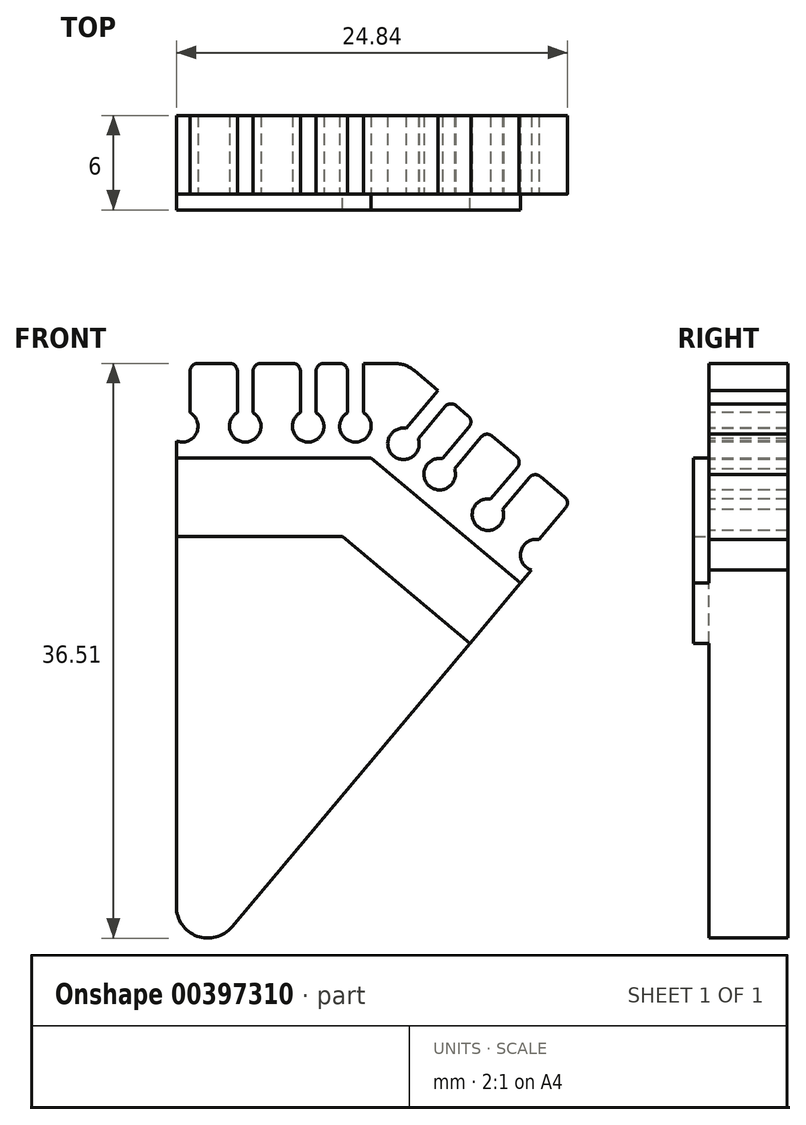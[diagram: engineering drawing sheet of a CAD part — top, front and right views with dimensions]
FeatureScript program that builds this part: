
annotation { "Feature Type Name" : "Feature", "Feature Type Description" : "" }
export const myFeature = defineFeature(function(context is Context, id is Id, definition is map)
    precondition{}
    {
        {
            var Q0;
            Q0=qCreatedBy(makeId("Front.planeOp"),FACE);
            var sketch = newSketch(context, id + "F0", { "sketchPlane" : qUnion([Q0])});
            skLineSegment(sketch, "E0.bottom", {"start": v(0, 0) * mm, "end": v(14.56, 0) * mm});
            skLineSegment(sketch, "E0.top", {"start": v(0, 40) * mm, "end": v(14.56, 40) * mm});
            skLineSegment(sketch, "E0.left", {"start": v(0, 0) * mm, "end": v(0, 40) * mm});
            skLineSegment(sketch, "E0.right", {"start": v(14.56, 0) * mm, "end": v(14.56, 40) * mm});
            skLineSegment(sketch, "E1", {"start": v(0, 0) * mm, "end": v(14.56, 40) * mm});
            skLineSegment(sketch, "E2", {"start": v(0, 34) * mm, "end": v(12.37, 34) * mm});
            skLineSegment(sketch, "E3", {"start": v(0, 29) * mm, "end": v(10.56, 29) * mm});
            skLineSegment(sketch, "E4", {"start": v(0, 38) * mm, "end": v(14.56, 38) * mm, "construction": true});
            skLineSegment(sketch, "E5", {"start": v(0, 36) * mm, "end": v(14.56, 36) * mm, "construction": true});
            skLineSegment(sketch, "E6", {"start": v(12.37, 34) * mm, "end": v(12.37, 40) * mm, "construction": true});
            skLineSegment(sketch, "E7", {"start": v(8.37, 34) * mm, "end": v(8.37, 40) * mm, "construction": true});
            skLineSegment(sketch, "E8", {"start": v(4.37, 34) * mm, "end": v(4.37, 40) * mm, "construction": true});
            skLineSegment(sketch, "E9", {"start": v(0.37, 34) * mm, "end": v(0.37, 40) * mm, "construction": true});
            skPoint(sketch, "E10", {"position": v(8.37, 36) * mm});
            skPoint(sketch, "E11", {"position": v(4.37, 36) * mm});
            skPoint(sketch, "E12", {"position": v(0.37, 36) * mm});
            skLineSegment(sketch, "E13", {"start": v(11.37, 34) * mm, "end": v(11.37, 40) * mm, "construction": true});
            skPoint(sketch, "E14", {"position": v(11.37, 36) * mm});
            skSolve(sketch);
        }
        {
            var Q0;
            Q0=qCreatedBy(makeId("Front.planeOp"),FACE);
            var sketch = newSketch(context, id + "F1", { "sketchPlane" : qUnion([Q0])});
            skCircle(sketch, "E15", {"center": v(11.37, 36) * mm, "radius": 1 * mm});
            skCircle(sketch, "E16", {"center": v(8.37, 36) * mm, "radius": 1 * mm});
            skCircle(sketch, "E17", {"center": v(0.37, 36) * mm, "radius": 1 * mm});
            skCircle(sketch, "E18", {"center": v(4.37, 36) * mm, "radius": 1 * mm});
            skLineSegment(sketch, "E19", {"start": v(10.87, 36.87) * mm, "end": v(10.87, 40) * mm});
            skLineSegment(sketch, "E20.MirrorCS", {"start": v(11.87, 36.87) * mm, "end": v(11.87, 40) * mm});
            skLineSegment(sketch, "E21", {"start": v(0.87, 36.87) * mm, "end": v(0.87, 40) * mm});
            skLineSegment(sketch, "E22", {"start": v(4.87, 36.87) * mm, "end": v(4.87, 40) * mm});
            skLineSegment(sketch, "E23.MirrorCS", {"start": v(3.87, 36.87) * mm, "end": v(3.87, 40) * mm});
            skLineSegment(sketch, "E24.MirrorCS", {"start": v(-0.13, 36.87) * mm, "end": v(-0.13, 40) * mm});
            skLineSegment(sketch, "E25", {"start": v(-0.13, 40) * mm, "end": v(0.87, 40) * mm});
            skLineSegment(sketch, "E26", {"start": v(3.87, 40) * mm, "end": v(4.87, 40) * mm});
            skLineSegment(sketch, "E27", {"start": v(7.87, 40) * mm, "end": v(8.87, 40) * mm});
            skLineSegment(sketch, "E28", {"start": v(10.87, 40) * mm, "end": v(11.87, 40) * mm});
            skLineSegment(sketch, "E29", {"start": v(8.87, 40) * mm, "end": v(8.87, 36.87) * mm});
            skLineSegment(sketch, "E30", {"start": v(7.87, 40) * mm, "end": v(7.87, 36.87) * mm});
            skSolve(sketch);
        }
        {
            var Q0;
            {var subQ3=sQuery(id+"F0.wireOp",EDGE,"E3");Q0=makeQuery(id+"F0.imprint","IMPRINT",FACE,{"disambiguationData":[TD([[makeQuery(id+"F0.imprint","IMPRINT",EDGE,{"derivedFrom":subQ3}),-1.0]])]});}
            var Q1;
            {var subQ0=sQuery(id+"F0.wireOp",EDGE,"E2");Q1=makeQuery(id+"F0.imprint","IMPRINT",FACE,{"disambiguationData":[TD([[makeQuery(id+"F0.imprint","IMPRINT",EDGE,{"derivedFrom":subQ0}),-1.0]])]});}
            var Q2;
            {var subQ0=sQuery(id+"F0.wireOp",EDGE,"E0.top");Q2=makeQuery(id+"F0.imprint","IMPRINT",FACE,{"disambiguationData":[TD([[makeQuery(id+"F0.imprint","IMPRINT",EDGE,{"derivedFrom":subQ0}),-1.0]])]});}
            extrude(context, id + "F2", {"entities" : qUnion([Q0, Q1, Q2]), "oppositeDirection" : true, "depth" : 5 * mm});
        }
        {
            var Q0;
            {var subQ0=sQuery(id+"F0.wireOp",EDGE,"E2");Q0=makeQuery(id+"F0.imprint","IMPRINT",FACE,{"disambiguationData":[TD([[makeQuery(id+"F0.imprint","IMPRINT",EDGE,{"derivedFrom":subQ0}),-1.0]])]});}
            extrude(context, id + "F3", {"entities" : qUnion([Q0]), "depth" : 1 * mm});
        }
        {
            var Q0;
            {var subQ0=sQuery(id+"F1.wireOp",EDGE,"E17");var subQ1=makeQuery(id+"F1.imprint","INTERSECT",VERTEX,{"derivedFrom":[subQ0,sQuery(id+"F1.wireOp",EDGE,"E21")]});Q0=makeQuery(id+"F1.imprint","IMPRINT",FACE,{"disambiguationData":[TD([[makeQuery(id+"F1.imprint","IMPRINT",EDGE,{"disambiguationData":[TD([[subQ1,-1.0]])],"derivedFrom":subQ0}),1.0]])]});}
            var Q1;
            {var subQ0=sQuery(id+"F1.wireOp",EDGE,"E21");Q1=makeQuery(id+"F1.imprint","IMPRINT",FACE,{"disambiguationData":[TD([[makeQuery(id+"F1.imprint","IMPRINT",EDGE,{"derivedFrom":subQ0}),1.0]])]});}
            var Q2;
            {var subQ0=sQuery(id+"F1.wireOp",EDGE,"E18");var subQ1=makeQuery(id+"F1.imprint","INTERSECT",VERTEX,{"derivedFrom":[subQ0,sQuery(id+"F1.wireOp",EDGE,"E22")]});Q2=makeQuery(id+"F1.imprint","IMPRINT",FACE,{"disambiguationData":[TD([[makeQuery(id+"F1.imprint","IMPRINT",EDGE,{"disambiguationData":[TD([[subQ1,-1.0]])],"derivedFrom":subQ0}),1.0]])]});}
            var Q3;
            {var subQ0=sQuery(id+"F1.wireOp",EDGE,"E22");Q3=makeQuery(id+"F1.imprint","IMPRINT",FACE,{"disambiguationData":[TD([[makeQuery(id+"F1.imprint","IMPRINT",EDGE,{"derivedFrom":subQ0}),1.0]])]});}
            var Q4;
            {var subQ0=sQuery(id+"F1.wireOp",EDGE,"E15");var subQ1=makeQuery(id+"F1.imprint","INTERSECT",VERTEX,{"derivedFrom":[subQ0,sQuery(id+"F1.wireOp",EDGE,"E19")]});Q4=makeQuery(id+"F1.imprint","IMPRINT",FACE,{"disambiguationData":[TD([[makeQuery(id+"F1.imprint","IMPRINT",EDGE,{"disambiguationData":[TD([[subQ1,-1.0]])],"derivedFrom":subQ0}),1.0]])]});}
            var Q5;
            {var subQ0=sQuery(id+"F1.wireOp",EDGE,"E16");var subQ1=makeQuery(id+"F1.imprint","INTERSECT",VERTEX,{"derivedFrom":[subQ0,sQuery(id+"F1.wireOp",EDGE,"E29")]});Q5=makeQuery(id+"F1.imprint","IMPRINT",FACE,{"disambiguationData":[TD([[makeQuery(id+"F1.imprint","IMPRINT",EDGE,{"disambiguationData":[TD([[subQ1,-1.0]])],"derivedFrom":subQ0}),1.0]])]});}
            var Q6;
            Q6=makeQuery(id+"F1.imprint","IMPRINT",FACE,{"disambiguationData":[TD([[makeQuery(id+"F1.imprint","IMPRINT",EDGE,{"derivedFrom":sQuery(id+"F1.wireOp",EDGE,"E27")}),-1.0]])]});
            var Q7;
            {var subQ0=sQuery(id+"F1.wireOp",EDGE,"E19");Q7=makeQuery(id+"F1.imprint","IMPRINT",FACE,{"disambiguationData":[TD([[makeQuery(id+"F1.imprint","IMPRINT",EDGE,{"derivedFrom":subQ0}),-1.0]])]});}
            extrude(context, id + "F4", {"entities" : qUnion([Q0, Q1, Q2, Q3, Q4, Q5, Q6, Q7]), "operationType" : NewBodyOperationType.REMOVE, "endBound" : BoundingType.UP_TO_NEXT, "oppositeDirection" : true, "depth" : 25 * mm});
        }
        {
            var Q0;
            Q0=makeQuery(id+"F4.boolean.opBoolean","COPY",EDGE,{"derivedFrom":makeQuery(id+"F4.opExtrude","SWEPT_EDGE",EDGE,{"disambiguationData":[OSD([sQuery(id+"F1.wireOp",EDGE,"E24.MirrorCS"),sQuery(id+"F1.wireOp",EDGE,"E25")])]})});
            var Q1;
            Q1=makeQuery(id+"F4.boolean.opBoolean","COPY",EDGE,{"derivedFrom":makeQuery(id+"F4.opExtrude","SWEPT_EDGE",EDGE,{"disambiguationData":[OSD([sQuery(id+"F1.wireOp",EDGE,"E21"),sQuery(id+"F1.wireOp",EDGE,"E25")])]})});
            var Q2;
            Q2=makeQuery(id+"F4.boolean.opBoolean","COPY",EDGE,{"derivedFrom":makeQuery(id+"F4.opExtrude","SWEPT_EDGE",EDGE,{"disambiguationData":[OSD([sQuery(id+"F1.wireOp",EDGE,"E23.MirrorCS"),sQuery(id+"F1.wireOp",EDGE,"E26")])]})});
            var Q3;
            Q3=makeQuery(id+"F4.boolean.opBoolean","COPY",EDGE,{"derivedFrom":makeQuery(id+"F4.opExtrude","SWEPT_EDGE",EDGE,{"disambiguationData":[OSD([sQuery(id+"F1.wireOp",EDGE,"E22"),sQuery(id+"F1.wireOp",EDGE,"E26")])]})});
            var Q4;
            Q4=makeQuery(id+"F4.boolean.opBoolean","COPY",EDGE,{"derivedFrom":makeQuery(id+"F4.opExtrude","SWEPT_EDGE",EDGE,{"disambiguationData":[OSD([sQuery(id+"F1.wireOp",EDGE,"18832a47-b105-4430-ba8b-26a2818898a60.MirrorCS"),sQuery(id+"F1.wireOp",EDGE,"E27")])]})});
            var Q5;
            Q5=makeQuery(id+"F4.boolean.opBoolean","COPY",EDGE,{"derivedFrom":makeQuery(id+"F4.opExtrude","SWEPT_EDGE",EDGE,{"disambiguationData":[OSD([sQuery(id+"F1.wireOp",EDGE,"63NlCEZY-h36I-1J4j-9E3q-yPAqCgqpdpVk"),sQuery(id+"F1.wireOp",EDGE,"E27")])]})});
            var Q6;
            Q6=makeQuery(id+"F4.boolean.opBoolean","COPY",EDGE,{"derivedFrom":makeQuery(id+"F4.opExtrude","SWEPT_EDGE",EDGE,{"disambiguationData":[OSD([sQuery(id+"F1.wireOp",EDGE,"E20.MirrorCS"),sQuery(id+"F1.wireOp",EDGE,"E28")])]})});
            var Q7;
            Q7=makeQuery(id+"F4.boolean.opBoolean","COPY",EDGE,{"derivedFrom":makeQuery(id+"F4.opExtrude","SWEPT_EDGE",EDGE,{"disambiguationData":[OSD([sQuery(id+"F1.wireOp",EDGE,"E19"),sQuery(id+"F1.wireOp",EDGE,"E28")])]})});
            fillet(context, id + "F5", {"entities" : qUnion([Q0, Q1, Q2, Q3, Q4, Q5, Q6, Q7]), "radius" : 0.5 * mm, "tangentPropagation" : true, "allowEdgeOverflow" : false});
        }
        {
            var Q0;
            Q0=makeQuery(id+"F2.opExtrude","SWEPT_BODY",BODY,{"disambiguationData":[OSD([sQuery(id+"F0.wireOp",EDGE,"E0.top"),sQuery(id+"F0.wireOp",EDGE,"E0.left"),sQuery(id+"F0.wireOp",EDGE,"E1")])]});
            var Q1;
            Q1=makeQuery(id+"F2.opExtrude","SWEPT_FACE",FACE,{"disambiguationData":[OSD([sQuery(id+"F0.wireOp",EDGE,"E1")])]});
            mirror(context, id + "F6", {"operationType" : NewBodyOperationType.ADD, "entities" : qUnion([Q0]), "mirrorPlane" : qUnion([Q1])});
        }
        {
            var Q0;
            Q0=makeQuery(id+"F3.opExtrude","SWEPT_BODY",BODY,{"disambiguationData":[OSD([sQuery(id+"F0.wireOp",EDGE,"E0.left"),sQuery(id+"F0.wireOp",EDGE,"E1"),sQuery(id+"F0.wireOp",EDGE,"E2"),sQuery(id+"F0.wireOp",EDGE,"E3")])]});
            var Q1;
            Q1=makeQuery(id+"F3.opExtrude","SWEPT_FACE",FACE,{"disambiguationData":[OSD([sQuery(id+"F0.wireOp",EDGE,"E1")])]});
            mirror(context, id + "F7", {"operationType" : NewBodyOperationType.ADD, "entities" : qUnion([Q0]), "mirrorPlane" : qUnion([Q1])});
        }
        {
            var Q0;
            {var subQ0=makeQuery(id+"F2.opExtrude","SWEPT_EDGE",EDGE,{"disambiguationData":[OSD([sQuery(id+"F0.wireOp",EDGE,"E0.top"),sQuery(id+"F0.wireOp",EDGE,"E0.right"),sQuery(id+"F0.wireOp",EDGE,"E1")])]});Q0=makeQuery(id+"F6.boolean.opBoolean","MERGE",EDGE,{"derivedFrom":[subQ0,makeQuery(id+"F6.opPattern","COPY",EDGE,{"derivedFrom":subQ0,"instanceName":"1"})]});}
            var Q1;
            {var subQ0=makeQuery(id+"F2.opExtrude","SWEPT_EDGE",EDGE,{"disambiguationData":[OSD([sQuery(id+"F0.wireOp",EDGE,"E0.bottom"),sQuery(id+"F0.wireOp",EDGE,"E0.left"),sQuery(id+"F0.wireOp",EDGE,"E1")])]});Q1=makeQuery(id+"F6.boolean.opBoolean","MERGE",EDGE,{"derivedFrom":[subQ0,makeQuery(id+"F6.opPattern","COPY",EDGE,{"derivedFrom":subQ0,"instanceName":"1"})]});}
            var Q2;
            Q2=makeQuery(id+"F6.opPattern","COPY",EDGE,{"derivedFrom":makeQuery(id+"F2.opExtrude","SWEPT_EDGE",EDGE,{"disambiguationData":[OSD([sQuery(id+"F0.wireOp",EDGE,"E0.top"),sQuery(id+"F0.wireOp",EDGE,"E0.left")])]}),"instanceName":"1"});
            var Q3;
            Q3=makeQuery(id+"F2.opExtrude","SWEPT_EDGE",EDGE,{"disambiguationData":[OSD([sQuery(id+"F0.wireOp",EDGE,"E0.top"),sQuery(id+"F0.wireOp",EDGE,"E0.left")])]});
            fillet(context, id + "F8", {"entities" : qUnion([Q0, Q1, Q2, Q3]), "radius" : 2 * mm, "tangentPropagation" : true, "allowEdgeOverflow" : false});
        }
    });
